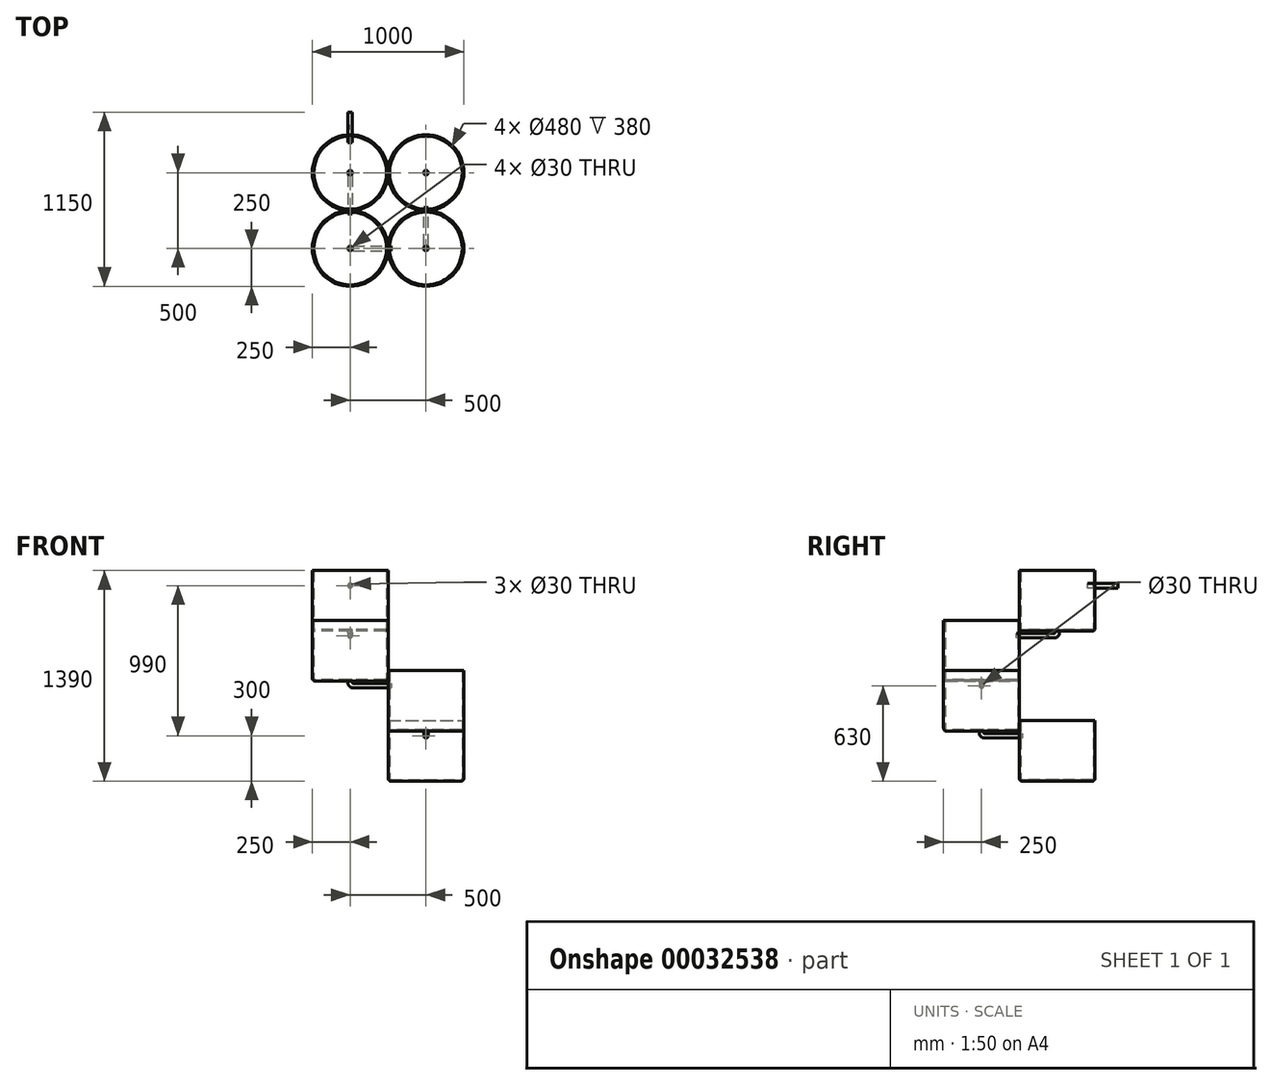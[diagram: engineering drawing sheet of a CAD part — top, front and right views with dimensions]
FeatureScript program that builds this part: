
annotation { "Feature Type Name" : "Feature", "Feature Type Description" : "" }
export const myFeature = defineFeature(function(context is Context, id is Id, definition is map)
    precondition{}
    {
        {
            var Q0;
            Q0=qCreatedBy(makeId("Top.planeOp"),FACE);
            var sketch = newSketch(context, id + "F0", { "sketchPlane" : qUnion([Q0])});
            skCircle(sketch, "E0", {"center": v(0, 0) * mm, "radius": 250 * mm});
            skSolve(sketch);
        }
        {
            var Q0;
            Q0=makeQuery(id+"F0.imprint","IMPRINT",FACE,{"disambiguationData":[TD([[makeQuery(id+"F0.imprint","IMPRINT",EDGE,{"derivedFrom":sQuery(id+"F0.wireOp",EDGE,"E0")}),1.0]])]});
            extrude(context, id + "F1", {"entities" : qUnion([Q0]), "depth" : 400 * mm});
        }
        {
            var Q0;
            Q0=makeQuery(id+"F1.opExtrude","CAP_EDGE",EDGE,{"disambiguationData":[OSD([sQuery(id+"F0.wireOp",EDGE,"E0")])],"isStart":true});
            fillet(context, id + "F2", {"entities" : qUnion([Q0]), "radius" : 20 * mm, "tangentPropagation" : true, "allowEdgeOverflow" : false});
        }
        {
            var Q0;
            Q0=makeQuery(id+"F1.opExtrude","CAP_FACE",FACE,{"disambiguationData":[OSD([sQuery(id+"F0.wireOp",EDGE,"E0")])],"isStart":false});
            shell(context, id + "F3", {"entities" : qUnion([Q0]), "thickness" : 10 * mm});
        }
        {
            var Q0;
            Q0=qCreatedBy(makeId("Front.planeOp"),FACE);
            var sketch = newSketch(context, id + "F4", { "sketchPlane" : qUnion([Q0])});
            skLineSegment(sketch, "E1.0", {"start": v(-250, 400) * mm, "end": v(250, 400) * mm, "construction": true});
            skLineSegment(sketch, "E2", {"start": v(0, 400) * mm, "end": v(0, 0) * mm, "construction": true});
            skCircle(sketch, "E3", {"center": v(0, 300) * mm, "radius": 15 * mm});
            skSolve(sketch);
        }
        {
            var Q0;
            Q0=makeQuery(id+"F4.imprint","IMPRINT",FACE,{"disambiguationData":[TD([[makeQuery(id+"F4.imprint","IMPRINT",EDGE,{"derivedFrom":sQuery(id+"F4.wireOp",EDGE,"E3")}),1.0]])]});
            extrude(context, id + "F5", {"entities" : qUnion([Q0]), "operationType" : NewBodyOperationType.REMOVE, "endBound" : BoundingType.THROUGH_ALL, "oppositeDirection" : true, "depth" : 589.9 * mm});
        }
        {
            var Q0;
            {var subQ0=sQuery(id+"F0.wireOp",EDGE,"E0");Q0=makeQuery(id+"F3.opShell","OFFSET_FACE",FACE,{"disambiguationData":[OSD([subQ0]),TDD([makeQuery(id+"F1.opExtrude","CAP_FACE",FACE,{"disambiguationData":[OSD([subQ0])],"isStart":true})])]});}
            var sketch = newSketch(context, id + "F6", { "sketchPlane" : qUnion([Q0])});
            skCircle(sketch, "E4", {"center": v(0, 0) * mm, "radius": 15 * mm});
            skSolve(sketch);
        }
        {
            var Q0;
            Q0=makeQuery(id+"F6.imprint","IMPRINT",FACE,{"disambiguationData":[TD([[makeQuery(id+"F6.imprint","IMPRINT",EDGE,{"derivedFrom":sQuery(id+"F6.wireOp",EDGE,"E4")}),1.0]])]});
            extrude(context, id + "F7", {"entities" : qUnion([Q0]), "operationType" : NewBodyOperationType.REMOVE, "endBound" : BoundingType.THROUGH_ALL, "oppositeDirection" : true, "depth" : 25 * mm});
        }
        {
            var Q0;
            Q0=makeQuery(id+"F4.imprint","IMPRINT",FACE,{"disambiguationData":[TD([[makeQuery(id+"F4.imprint","IMPRINT",EDGE,{"derivedFrom":sQuery(id+"F4.wireOp",EDGE,"E3")}),1.0]])]});
            var Q1;
            {var subQ0=sQuery(id+"F0.wireOp",EDGE,"E0");Q1=makeQuery(id+"F3.opShell","OFFSET_FACE",FACE,{"disambiguationData":[OSD([subQ0]),TDD([makeQuery(id+"F1.opExtrude","SWEPT_FACE",FACE,{"disambiguationData":[OSD([subQ0])]})])]});}
            extrude(context, id + "F8", {"entities" : qUnion([Q0]), "oppositeDirection" : true, "depth" : 400 * mm, "hasSecondDirection" : true, "secondDirectionOppositeDirection" : true, "secondDirectionBoundEntityFace" : qUnion([Q1]), "secondDirectionDepth" : 200 * mm});
        }
        {
            var Q0;
            Q0=makeQuery(id+"F6.imprint","IMPRINT",FACE,{"disambiguationData":[TD([[makeQuery(id+"F6.imprint","IMPRINT",EDGE,{"derivedFrom":sQuery(id+"F6.wireOp",EDGE,"E4")}),1.0]])]});
            extrude(context, id + "F9", {"entities" : qUnion([Q0]), "oppositeDirection" : true, "depth" : 20 * mm});
        }
        {
            var Q0;
            Q0=qCreatedBy(makeId("Right.planeOp"),FACE);
            var sketch = newSketch(context, id + "F10", { "sketchPlane" : qUnion([Q0])});
            skLineSegment(sketch, "E5.0", {"start": v(-15, -10) * mm, "end": v(15, -10) * mm, "construction": true});
            skLineSegment(sketch, "E6", {"start": v(-20, -30) * mm, "end": v(-270, -30) * mm});
            skArc(sketch, "E7", {"start": v(-20, -30) * mm, "mid": v(-5.86, -24.14) * mm, "end": v(0, -10) * mm});
            skLineSegment(sketch, "E8", {"start": v(0, -10) * mm, "end": v(0, 7) * mm, "construction": true});
            skLineSegment(sketch, "E9.0", {"start": v(-250, 20) * mm, "end": v(250, 20) * mm, "construction": true});
            skSolve(sketch);
        }
        {
            var Q0;
            Q0=makeQuery(id+"F9.opExtrude","CAP_FACE",FACE,{"disambiguationData":[OSD([sQuery(id+"F6.wireOp",EDGE,"E4")])],"isStart":false});
            var Q1;
            Q1=sQuery(id+"F10.wireOp",EDGE,"E7");
            var Q2;
            Q2=sQuery(id+"F10.wireOp",EDGE,"E6");
            sweep(context, id + "F11", {"operationType" : NewBodyOperationType.ADD, "profiles" : qUnion([Q0]), "path" : qUnion([Q1, Q2])});
        }
        {
            var Q0;
            Q0=makeQuery(id+"F1.opExtrude","SWEPT_BODY",BODY,{"disambiguationData":[OSD([sQuery(id+"F0.wireOp",EDGE,"E0")])]});
            var Q1;
            Q1=makeQuery(id+"F9.opExtrude","SWEPT_BODY",BODY,{"disambiguationData":[OSD([sQuery(id+"F6.wireOp",EDGE,"E4")])]});
            transform(context, id + "F12", {"entities" : qUnion([Q0, Q1]), "transformType" : TransformType.TRANSLATION_3D, "dx" : 0 * mm, "dy" : -500 * mm, "dz" : -330 * mm, "makeCopy" : true});
        }
        {
            var Q0;
            Q0=makeQuery(id+"F12.opPattern","COPY",BODY,{"derivedFrom":makeQuery(id+"F1.opExtrude","SWEPT_BODY",BODY,{"disambiguationData":[OSD([sQuery(id+"F0.wireOp",EDGE,"E0")])]}),"instanceName":"1"});
            transform(context, id + "F13", {"entities" : qUnion([Q0]), "transformType" : TransformType.TRANSLATION_3D, "dx" : 0 * mm, "dy" : -500 * mm, "dz" : -330 * mm, "makeCopy" : true});
        }
        {
            var Q0;
            Q0=makeQuery(id+"F13.opPattern","COPY",BODY,{"derivedFrom":makeQuery(id+"F12.opPattern","COPY",BODY,{"derivedFrom":makeQuery(id+"F1.opExtrude","SWEPT_BODY",BODY,{"disambiguationData":[OSD([sQuery(id+"F0.wireOp",EDGE,"E0")])]}),"instanceName":"1"}),"instanceName":"1"});
            var Q1;
            Q1=makeQuery(id+"F12.opPattern","COPY",BODY,{"derivedFrom":makeQuery(id+"F9.opExtrude","SWEPT_BODY",BODY,{"disambiguationData":[OSD([sQuery(id+"F6.wireOp",EDGE,"E4")])]}),"instanceName":"1"});
            var Q2;
            {var subQ0=sQuery(id+"F0.wireOp",EDGE,"E0");Q2=makeQuery(id+"F12.opPattern","COPY",EDGE,{"derivedFrom":makeQuery(id+"F3.opShell","OFFSET_EDGE",EDGE,{"disambiguationData":[OSD([subQ0]),TDD([makeQuery(id+"F1.opExtrude","CAP_EDGE",EDGE,{"disambiguationData":[OSD([subQ0])],"isStart":false})])]}),"instanceName":"1"});}
            transform(context, id + "F14", {"entities" : qUnion([Q0, Q1]), "transformType" : TransformType.ROTATION, "transformAxis" : qUnion([Q2]), "angle" : 90 * degree, "makeCopy" : false});
        }
        {
            var Q0;
            Q0=makeQuery(id+"F12.opPattern","COPY",BODY,{"derivedFrom":makeQuery(id+"F9.opExtrude","SWEPT_BODY",BODY,{"disambiguationData":[OSD([sQuery(id+"F6.wireOp",EDGE,"E4")])]}),"instanceName":"1"});
            var Q1;
            Q1=makeQuery(id+"F13.opPattern","COPY",BODY,{"derivedFrom":makeQuery(id+"F12.opPattern","COPY",BODY,{"derivedFrom":makeQuery(id+"F1.opExtrude","SWEPT_BODY",BODY,{"disambiguationData":[OSD([sQuery(id+"F0.wireOp",EDGE,"E0")])]}),"instanceName":"1"}),"instanceName":"1"});
            transform(context, id + "F15", {"entities" : qUnion([Q0, Q1]), "transformType" : TransformType.TRANSLATION_3D, "dx" : 500 * mm, "dy" : 0 * mm, "dz" : -330 * mm, "makeCopy" : true});
        }
        {
            var Q0;
            Q0=makeQuery(id+"F15.opPattern","COPY",BODY,{"derivedFrom":makeQuery(id+"F13.opPattern","COPY",BODY,{"derivedFrom":makeQuery(id+"F12.opPattern","COPY",BODY,{"derivedFrom":makeQuery(id+"F1.opExtrude","SWEPT_BODY",BODY,{"disambiguationData":[OSD([sQuery(id+"F0.wireOp",EDGE,"E0")])]}),"instanceName":"1"}),"instanceName":"1"}),"instanceName":"1"});
            var Q1;
            Q1=makeQuery(id+"F15.opPattern","COPY",BODY,{"derivedFrom":makeQuery(id+"F12.opPattern","COPY",BODY,{"derivedFrom":makeQuery(id+"F9.opExtrude","SWEPT_BODY",BODY,{"disambiguationData":[OSD([sQuery(id+"F6.wireOp",EDGE,"E4")])]}),"instanceName":"1"}),"instanceName":"1"});
            var Q2;
            {var subQ0=sQuery(id+"F0.wireOp",EDGE,"E0");Q2=makeQuery(id+"F13.opPattern","COPY",EDGE,{"derivedFrom":makeQuery(id+"F12.opPattern","COPY",EDGE,{"derivedFrom":makeQuery(id+"F3.opShell","OFFSET_EDGE",EDGE,{"disambiguationData":[OSD([subQ0]),TDD([makeQuery(id+"F1.opExtrude","CAP_EDGE",EDGE,{"disambiguationData":[OSD([subQ0])],"isStart":false})])]}),"instanceName":"1"}),"instanceName":"1"});}
            transform(context, id + "F16", {"entities" : qUnion([Q0, Q1]), "transformType" : TransformType.ROTATION, "transformAxis" : qUnion([Q2]), "angle" : 90 * degree, "makeCopy" : false});
        }
    });
